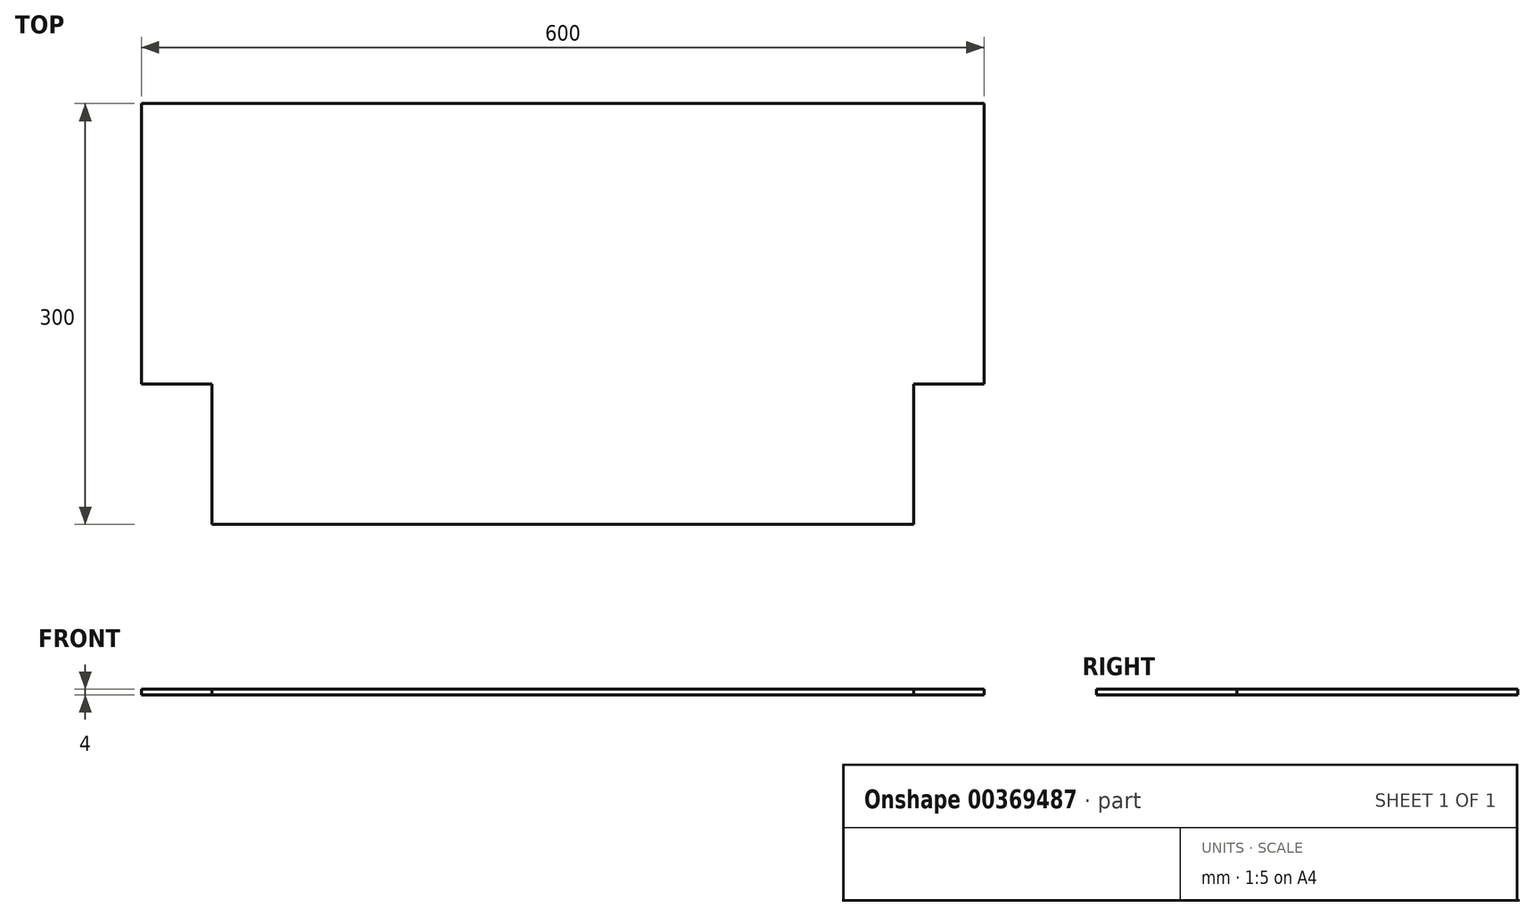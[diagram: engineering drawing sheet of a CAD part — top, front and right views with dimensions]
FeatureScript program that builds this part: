
annotation { "Feature Type Name" : "Feature", "Feature Type Description" : "" }
export const myFeature = defineFeature(function(context is Context, id is Id, definition is map)
    precondition{}
    {
        {
            var Q0;
            Q0=qCreatedBy(makeId("Top.planeOp"),FACE);
            var sketch = newSketch(context, id + "F0", { "sketchPlane" : qUnion([Q0])});
            skLineSegment(sketch, "E0", {"start": v(-291.68, 91.96) * mm, "end": v(308.32, 91.96) * mm});
            skLineSegment(sketch, "E1", {"start": v(308.32, 91.96) * mm, "end": v(308.32, -108.04) * mm});
            skLineSegment(sketch, "E2", {"start": v(308.32, -108.04) * mm, "end": v(258.32, -108.04) * mm});
            skLineSegment(sketch, "E3", {"start": v(258.32, -108.04) * mm, "end": v(258.32, -208.04) * mm});
            skLineSegment(sketch, "E4", {"start": v(258.32, -208.04) * mm, "end": v(-241.68, -208.04) * mm});
            skLineSegment(sketch, "E5", {"start": v(-241.68, -208.04) * mm, "end": v(-241.68, -108.04) * mm});
            skLineSegment(sketch, "E6", {"start": v(-241.68, -108.04) * mm, "end": v(-279.9, -108.04) * mm});
            skLineSegment(sketch, "E7", {"start": v(-279.9, -108.04) * mm, "end": v(-291.68, -108.04) * mm});
            skLineSegment(sketch, "E8", {"start": v(-291.68, -108.04) * mm, "end": v(-291.68, 91.96) * mm});
            skSolve(sketch);
        }
        {
            var Q0;
            Q0=makeQuery(id+"F0.imprint","IMPRINT",FACE,{"disambiguationData":[TD([[makeQuery(id+"F0.imprint","IMPRINT",EDGE,{"derivedFrom":sQuery(id+"F0.wireOp",EDGE,"E0")}),-1.0]])]});
            extrude(context, id + "F1", {"entities" : qUnion([Q0]), "depth" : 4 * mm});
        }
    });
